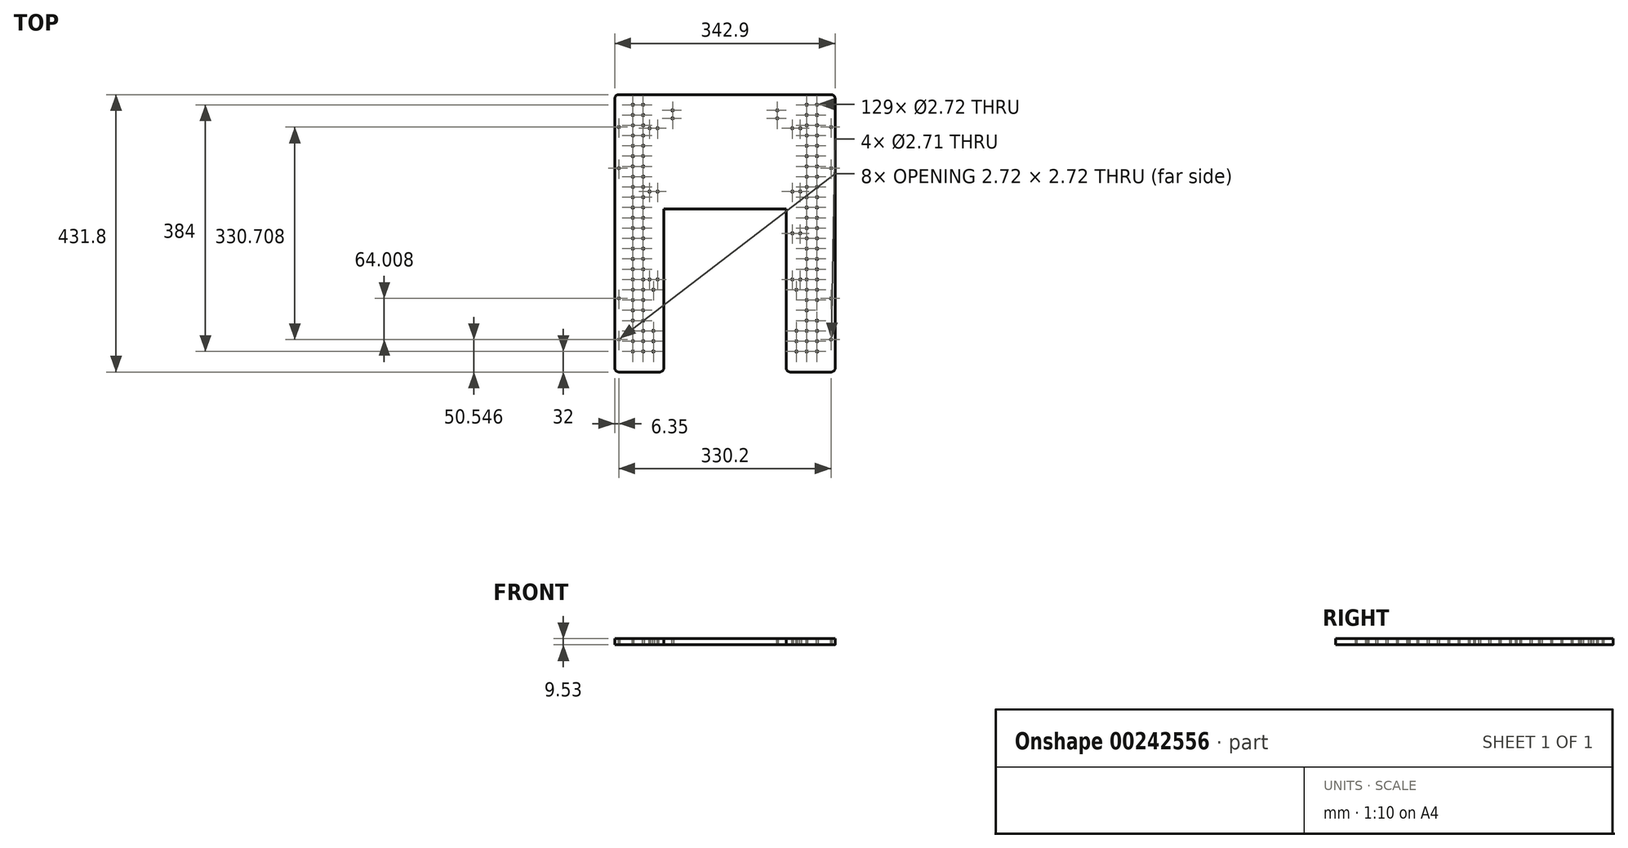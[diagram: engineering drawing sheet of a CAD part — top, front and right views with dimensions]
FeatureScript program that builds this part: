
annotation { "Feature Type Name" : "Feature", "Feature Type Description" : "" }
export const myFeature = defineFeature(function(context is Context, id is Id, definition is map)
    precondition{}
    {
        {
            var Q0;
            Q0=qCreatedBy(makeId("Top.planeOp"),FACE);
            var sketch = newSketch(context, id + "F0", { "sketchPlane" : qUnion([Q0])});
            skLineSegment(sketch, "E0.bottom", {"start": v(228.6, 228.6) * mm, "end": v(-228.6, 228.6) * mm, "construction": true});
            skLineSegment(sketch, "E0.top", {"start": v(228.6, -228.6) * mm, "end": v(-228.6, -228.6) * mm, "construction": true});
            skLineSegment(sketch, "E0.left", {"start": v(228.6, 228.6) * mm, "end": v(228.6, -228.6) * mm, "construction": true});
            skLineSegment(sketch, "E0.right", {"start": v(-228.6, 228.6) * mm, "end": v(-228.6, -228.6) * mm, "construction": true});
            skPoint(sketch, "E0.middle", {"position": v(0, 0) * mm});
            skLineSegment(sketch, "E1.bottom", {"start": v(-165.1, 215.9) * mm, "end": v(-101.6, 215.9) * mm});
            skLineSegment(sketch, "E1.top", {"start": v(-165.1, -215.9) * mm, "end": v(-101.6, -215.9) * mm});
            skLineSegment(sketch, "E1.left", {"start": v(-171.45, 209.55) * mm, "end": v(-171.45, -209.55) * mm});
            skLineSegment(sketch, "E1.right", {"start": v(-95.25, 209.55) * mm, "end": v(-95.25, -209.55) * mm});
            skLineSegment(sketch, "E2.bottom", {"start": v(-95.25, 215.9) * mm, "end": v(0, 215.9) * mm});
            skLineSegment(sketch, "E2.top", {"start": v(-95.25, 38.1) * mm, "end": v(0, 38.1) * mm});
            skLineSegment(sketch, "E2.left", {"start": v(-95.25, 215.9) * mm, "end": v(-95.25, 38.1) * mm});
            skLineSegment(sketch, "E2.right", {"start": v(0, 215.9) * mm, "end": v(0, 38.1) * mm});
            skLineSegment(sketch, "E3.MirrorCS", {"start": v(95.25, 215.9) * mm, "end": v(0, 215.9) * mm});
            skLineSegment(sketch, "E4.MirrorCS", {"start": v(95.25, 38.1) * mm, "end": v(0, 38.1) * mm});
            skLineSegment(sketch, "E5.MirrorCS", {"start": v(95.25, 215.9) * mm, "end": v(95.25, 38.1) * mm});
            skLineSegment(sketch, "E6.MirrorCS", {"start": v(95.25, 209.55) * mm, "end": v(95.25, -209.55) * mm});
            skLineSegment(sketch, "E7.MirrorCS", {"start": v(171.45, 209.55) * mm, "end": v(171.45, -209.55) * mm});
            skLineSegment(sketch, "E8.MirrorCS", {"start": v(165.1, -215.9) * mm, "end": v(101.6, -215.9) * mm});
            skLineSegment(sketch, "E9.MirrorCS", {"start": v(165.1, 215.9) * mm, "end": v(101.6, 215.9) * mm});
            skPoint(sketch, "E10.visualSharp", {"position": v(-171.45, 215.9) * mm});
            skArc(sketch, "E10.filletArc", {"start": v(-165.1, 215.9) * mm, "mid": v(-169.6, 214.04) * mm, "end": v(-171.45, 209.55) * mm});
            skPoint(sketch, "E11.visualSharp", {"position": v(-95.25, 215.9) * mm});
            skPoint(sketch, "E12.visualSharp", {"position": v(-171.45, -215.9) * mm});
            skArc(sketch, "E12.filletArc", {"start": v(-171.45, -209.55) * mm, "mid": v(-169.6, -214.04) * mm, "end": v(-165.1, -215.9) * mm});
            skPoint(sketch, "E13.visualSharp", {"position": v(-95.25, -215.9) * mm});
            skArc(sketch, "E13.filletArc", {"start": v(-101.6, -215.9) * mm, "mid": v(-97.1, -214.04) * mm, "end": v(-95.25, -209.55) * mm});
            skPoint(sketch, "E14.visualSharp", {"position": v(95.25, -215.9) * mm});
            skArc(sketch, "E14.filletArc", {"start": v(95.25, -209.55) * mm, "mid": v(97.1, -214.04) * mm, "end": v(101.6, -215.9) * mm});
            skPoint(sketch, "E15.visualSharp", {"position": v(171.45, -215.9) * mm});
            skArc(sketch, "E15.filletArc", {"start": v(165.1, -215.9) * mm, "mid": v(169.6, -214.04) * mm, "end": v(171.45, -209.55) * mm});
            skPoint(sketch, "E16.visualSharp", {"position": v(171.45, 215.9) * mm});
            skArc(sketch, "E16.filletArc", {"start": v(171.45, 209.55) * mm, "mid": v(169.6, 214.04) * mm, "end": v(165.1, 215.9) * mm});
            skPoint(sketch, "E17.visualSharp", {"position": v(95.25, 215.9) * mm});
            skCircle(sketch, "E18", {"center": v(-165.1, 165.35) * mm, "radius": 1.36 * mm});
            skCircle(sketch, "E19", {"center": v(-165.1, 101.35) * mm, "radius": 1.36 * mm});
            skPoint(sketch, "E20", {"position": v(-165.1, 133.35) * mm});
            skCircle(sketch, "E21.MirrorC", {"center": v(165.1, 165.35) * mm, "radius": 1.36 * mm});
            skCircle(sketch, "E22.MirrorC", {"center": v(165.1, 101.35) * mm, "radius": 1.36 * mm});
            skCircle(sketch, "E23.MirrorC", {"center": v(165.1, -101.35) * mm, "radius": 1.36 * mm});
            skCircle(sketch, "E24.MirrorC", {"center": v(165.1, -165.35) * mm, "radius": 1.36 * mm});
            skCircle(sketch, "E25.MirrorC", {"center": v(-165.1, -165.35) * mm, "radius": 1.36 * mm});
            skCircle(sketch, "E26.MirrorC", {"center": v(-165.1, -101.35) * mm, "radius": 1.36 * mm});
            skPoint(sketch, "E27", {"position": v(-111.25, -151.9) * mm});
            skPoint(sketch, "E28", {"position": v(-111.25, -87.9) * mm});
            skPoint(sketch, "E29", {"position": v(-111.25, -167.9) * mm});
            skPoint(sketch, "E30", {"position": v(-111.25, -183.9) * mm});
            skCircle(sketch, "E31", {"center": v(-117.25, 64.95) * mm, "radius": 1.36 * mm});
            skCircle(sketch, "E32", {"center": v(-111.25, -87.9) * mm, "radius": 1.36 * mm});
            skCircle(sketch, "E33", {"center": v(-111.25, -151.9) * mm, "radius": 1.36 * mm});
            skCircle(sketch, "E34", {"center": v(-111.25, -183.9) * mm, "radius": 1.36 * mm});
            skCircle(sketch, "E35", {"center": v(-111.25, -167.9) * mm, "radius": 1.36 * mm});
            skCircle(sketch, "E36", {"center": v(-104.75, 64.95) * mm, "radius": 1.36 * mm});
            skCircle(sketch, "E37", {"center": v(-117.25, -71.82) * mm, "radius": 1.36 * mm});
            skCircle(sketch, "E38", {"center": v(-104.75, -71.82) * mm, "radius": 1.36 * mm});
            skCircle(sketch, "E39", {"center": v(-117.25, 163.5) * mm, "radius": 1.36 * mm});
            skCircle(sketch, "E40", {"center": v(-104.75, 163.5) * mm, "radius": 1.36 * mm});
            skLineSegment(sketch, "E41", {"start": v(-101.6, 215.9) * mm, "end": v(-95.25, 215.9) * mm});
            skLineSegment(sketch, "E42", {"start": v(101.6, 215.9) * mm, "end": v(95.25, 215.9) * mm});
            skCircle(sketch, "E43", {"center": v(-81.47, 178.92) * mm, "radius": 1.36 * mm});
            skCircle(sketch, "E44", {"center": v(-81.47, 191.42) * mm, "radius": 1.36 * mm});
            skCircle(sketch, "E45.MirrorC", {"center": v(111.25, -183.9) * mm, "radius": 1.36 * mm});
            skCircle(sketch, "E46.MirrorC", {"center": v(111.25, -167.9) * mm, "radius": 1.36 * mm});
            skCircle(sketch, "E47.MirrorC", {"center": v(111.25, -151.9) * mm, "radius": 1.36 * mm});
            skCircle(sketch, "E48.MirrorC", {"center": v(111.25, -87.9) * mm, "radius": 1.36 * mm});
            skCircle(sketch, "E49.MirrorC", {"center": v(104.75, -71.82) * mm, "radius": 1.36 * mm});
            skCircle(sketch, "E50.MirrorC", {"center": v(117.25, -71.82) * mm, "radius": 1.36 * mm});
            skCircle(sketch, "E51.MirrorC", {"center": v(117.25, 0) * mm, "radius": 1.36 * mm});
            skCircle(sketch, "E52.MirrorC", {"center": v(104.75, 0) * mm, "radius": 1.36 * mm});
            skCircle(sketch, "E53.MirrorC", {"center": v(117.25, 64.95) * mm, "radius": 1.36 * mm});
            skCircle(sketch, "E54.MirrorC", {"center": v(104.75, 64.95) * mm, "radius": 1.36 * mm});
            skCircle(sketch, "E55.MirrorC", {"center": v(117.25, 163.5) * mm, "radius": 1.36 * mm});
            skCircle(sketch, "E56.MirrorC", {"center": v(104.75, 163.5) * mm, "radius": 1.36 * mm});
            skCircle(sketch, "E57.MirrorC", {"center": v(81.47, 178.92) * mm, "radius": 1.36 * mm});
            skCircle(sketch, "E58.MirrorC", {"center": v(81.47, 191.42) * mm, "radius": 1.36 * mm});
            skCircle(sketch, "E59.MirrorC", {"center": v(-143.25, -183.9) * mm, "radius": 1.36 * mm});
            skCircle(sketch, "E60.0.1.0", {"center": v(-143.25, -167.9) * mm, "radius": 1.36 * mm});
            skCircle(sketch, "E60.0.2.0", {"center": v(-143.25, -151.9) * mm, "radius": 1.36 * mm});
            skCircle(sketch, "E60.0.3.0", {"center": v(-143.25, -135.9) * mm, "radius": 1.36 * mm});
            skCircle(sketch, "E60.0.4.0", {"center": v(-143.25, -119.9) * mm, "radius": 1.36 * mm});
            skCircle(sketch, "E60.0.5.0", {"center": v(-143.25, -103.9) * mm, "radius": 1.36 * mm});
            skCircle(sketch, "E60.0.6.0", {"center": v(-143.25, -87.9) * mm, "radius": 1.36 * mm});
            skCircle(sketch, "E60.0.7.0", {"center": v(-143.25, -71.9) * mm, "radius": 1.36 * mm});
            skCircle(sketch, "E60.0.8.0", {"center": v(-143.25, -55.9) * mm, "radius": 1.36 * mm});
            skCircle(sketch, "E60.0.9.0", {"center": v(-143.25, -39.9) * mm, "radius": 1.36 * mm});
            skCircle(sketch, "E60.0.10.0", {"center": v(-143.25, -23.9) * mm, "radius": 1.36 * mm});
            skCircle(sketch, "E60.0.11.0", {"center": v(-143.25, -7.9) * mm, "radius": 1.36 * mm});
            skCircle(sketch, "E60.0.12.0", {"center": v(-143.25, 8.1) * mm, "radius": 1.36 * mm});
            skCircle(sketch, "E60.0.13.0", {"center": v(-143.25, 24.1) * mm, "radius": 1.36 * mm});
            skCircle(sketch, "E60.0.14.0", {"center": v(-143.25, 40.1) * mm, "radius": 1.36 * mm});
            skCircle(sketch, "E60.0.15.0", {"center": v(-143.25, 56.1) * mm, "radius": 1.36 * mm});
            skCircle(sketch, "E60.0.16.0", {"center": v(-143.25, 72.1) * mm, "radius": 1.36 * mm});
            skCircle(sketch, "E60.0.17.0", {"center": v(-143.25, 88.1) * mm, "radius": 1.36 * mm});
            skCircle(sketch, "E60.0.18.0", {"center": v(-143.25, 104.1) * mm, "radius": 1.36 * mm});
            skCircle(sketch, "E60.0.19.0", {"center": v(-143.25, 120.1) * mm, "radius": 1.36 * mm});
            skCircle(sketch, "E60.0.20.0", {"center": v(-143.25, 136.1) * mm, "radius": 1.36 * mm});
            skCircle(sketch, "E60.0.21.0", {"center": v(-143.25, 152.1) * mm, "radius": 1.36 * mm});
            skCircle(sketch, "E60.0.22.0", {"center": v(-143.25, 168.1) * mm, "radius": 1.36 * mm});
            skCircle(sketch, "E60.0.23.0", {"center": v(-143.25, 184.1) * mm, "radius": 1.36 * mm});
            skCircle(sketch, "E60.0.24.0", {"center": v(-143.25, 200.1) * mm, "radius": 1.36 * mm});
            skLineSegment(sketch, "E60.direction1", {"start": v(-143.25, -183.9) * mm, "end": v(-127.25, -183.9) * mm, "construction": true});
            skLineSegment(sketch, "E60.direction2", {"start": v(-143.25, -183.9) * mm, "end": v(-143.25, -167.9) * mm, "construction": true});
            skCircle(sketch, "E61.0.1.0", {"center": v(-127.25, -183.9) * mm, "radius": 1.36 * mm});
            skCircle(sketch, "E61.0.1.1", {"center": v(-127.25, -167.9) * mm, "radius": 1.36 * mm});
            skCircle(sketch, "E61.0.1.2", {"center": v(-127.25, -151.9) * mm, "radius": 1.36 * mm});
            skCircle(sketch, "E61.0.1.3", {"center": v(-127.25, -135.9) * mm, "radius": 1.36 * mm});
            skCircle(sketch, "E61.0.1.4", {"center": v(-127.25, -119.9) * mm, "radius": 1.36 * mm});
            skCircle(sketch, "E61.0.1.5", {"center": v(-127.25, -103.9) * mm, "radius": 1.36 * mm});
            skCircle(sketch, "E61.0.1.6", {"center": v(-127.25, -87.9) * mm, "radius": 1.36 * mm});
            skCircle(sketch, "E61.0.1.7", {"center": v(-127.25, -71.9) * mm, "radius": 1.36 * mm});
            skCircle(sketch, "E61.0.1.8", {"center": v(-127.25, -55.9) * mm, "radius": 1.36 * mm});
            skCircle(sketch, "E61.0.1.9", {"center": v(-127.25, -39.9) * mm, "radius": 1.36 * mm});
            skCircle(sketch, "E61.0.1.10", {"center": v(-127.25, -23.9) * mm, "radius": 1.36 * mm});
            skCircle(sketch, "E61.0.1.11", {"center": v(-127.25, -7.9) * mm, "radius": 1.36 * mm});
            skCircle(sketch, "E61.0.1.12", {"center": v(-127.25, 8.1) * mm, "radius": 1.36 * mm});
            skCircle(sketch, "E61.0.1.13", {"center": v(-127.25, 24.1) * mm, "radius": 1.36 * mm});
            skCircle(sketch, "E61.0.1.14", {"center": v(-127.25, 40.1) * mm, "radius": 1.36 * mm});
            skCircle(sketch, "E61.0.1.15", {"center": v(-127.25, 56.1) * mm, "radius": 1.36 * mm});
            skCircle(sketch, "E61.0.1.16", {"center": v(-127.25, 72.1) * mm, "radius": 1.36 * mm});
            skCircle(sketch, "E61.0.1.17", {"center": v(-127.25, 88.1) * mm, "radius": 1.36 * mm});
            skCircle(sketch, "E61.0.1.18", {"center": v(-127.25, 104.1) * mm, "radius": 1.36 * mm});
            skCircle(sketch, "E61.0.1.19", {"center": v(-127.25, 120.1) * mm, "radius": 1.36 * mm});
            skCircle(sketch, "E61.0.1.20", {"center": v(-127.25, 136.1) * mm, "radius": 1.36 * mm});
            skCircle(sketch, "E61.0.1.21", {"center": v(-127.25, 152.1) * mm, "radius": 1.36 * mm});
            skCircle(sketch, "E61.0.1.22", {"center": v(-127.25, 168.1) * mm, "radius": 1.36 * mm});
            skCircle(sketch, "E61.0.1.23", {"center": v(-127.25, 184.1) * mm, "radius": 1.36 * mm});
            skCircle(sketch, "E61.0.1.24", {"center": v(-127.25, 200.1) * mm, "radius": 1.36 * mm});
            skCircle(sketch, "E62.MirrorC", {"center": v(127.25, -183.9) * mm, "radius": 1.36 * mm});
            skCircle(sketch, "E63.MirrorC", {"center": v(143.25, -183.9) * mm, "radius": 1.36 * mm});
            skCircle(sketch, "E64.MirrorC", {"center": v(143.25, -167.9) * mm, "radius": 1.36 * mm});
            skCircle(sketch, "E65.MirrorC", {"center": v(127.25, -167.9) * mm, "radius": 1.36 * mm});
            skCircle(sketch, "E66.MirrorC", {"center": v(127.25, -151.9) * mm, "radius": 1.36 * mm});
            skCircle(sketch, "E67.MirrorC", {"center": v(143.25, -151.9) * mm, "radius": 1.36 * mm});
            skCircle(sketch, "E68.MirrorC", {"center": v(143.25, -135.9) * mm, "radius": 1.36 * mm});
            skCircle(sketch, "E69.MirrorC", {"center": v(127.25, -135.9) * mm, "radius": 1.36 * mm});
            skCircle(sketch, "E70.MirrorC", {"center": v(127.25, -119.9) * mm, "radius": 1.36 * mm});
            skCircle(sketch, "E71.MirrorC", {"center": v(127.25, -103.9) * mm, "radius": 1.36 * mm});
            skCircle(sketch, "E72.MirrorC", {"center": v(127.25, -87.9) * mm, "radius": 1.36 * mm});
            skCircle(sketch, "E73.MirrorC", {"center": v(143.25, -103.9) * mm, "radius": 1.36 * mm});
            skCircle(sketch, "E74.MirrorC", {"center": v(143.25, -87.9) * mm, "radius": 1.36 * mm});
            skCircle(sketch, "E75.MirrorC", {"center": v(143.25, -71.9) * mm, "radius": 1.36 * mm});
            skCircle(sketch, "E76.MirrorC", {"center": v(143.25, -55.9) * mm, "radius": 1.36 * mm});
            skCircle(sketch, "E77.MirrorC", {"center": v(127.25, -71.9) * mm, "radius": 1.36 * mm});
            skCircle(sketch, "E78.MirrorC", {"center": v(127.25, -55.9) * mm, "radius": 1.36 * mm});
            skCircle(sketch, "E79.MirrorC", {"center": v(143.25, -39.9) * mm, "radius": 1.36 * mm});
            skCircle(sketch, "E80.MirrorC", {"center": v(127.25, -39.9) * mm, "radius": 1.36 * mm});
            skCircle(sketch, "E81.MirrorC", {"center": v(143.25, -23.9) * mm, "radius": 1.36 * mm});
            skCircle(sketch, "E82.MirrorC", {"center": v(127.25, -23.9) * mm, "radius": 1.36 * mm});
            skCircle(sketch, "E83.MirrorC", {"center": v(127.25, -7.9) * mm, "radius": 1.36 * mm});
            skCircle(sketch, "E84.MirrorC", {"center": v(143.25, -7.9) * mm, "radius": 1.36 * mm});
            skCircle(sketch, "E85.MirrorC", {"center": v(143.25, 8.1) * mm, "radius": 1.36 * mm});
            skCircle(sketch, "E86.MirrorC", {"center": v(127.25, 8.1) * mm, "radius": 1.36 * mm});
            skCircle(sketch, "E87.MirrorC", {"center": v(127.25, 24.1) * mm, "radius": 1.36 * mm});
            skCircle(sketch, "E88.MirrorC", {"center": v(143.25, 24.1) * mm, "radius": 1.36 * mm});
            skCircle(sketch, "E89.MirrorC", {"center": v(143.25, 40.1) * mm, "radius": 1.36 * mm});
            skCircle(sketch, "E90.MirrorC", {"center": v(127.25, 40.1) * mm, "radius": 1.36 * mm});
            skCircle(sketch, "E91.MirrorC", {"center": v(127.25, 56.1) * mm, "radius": 1.36 * mm});
            skCircle(sketch, "E92.MirrorC", {"center": v(143.25, 56.1) * mm, "radius": 1.36 * mm});
            skCircle(sketch, "E93.MirrorC", {"center": v(143.25, 72.1) * mm, "radius": 1.36 * mm});
            skCircle(sketch, "E94.MirrorC", {"center": v(127.25, 72.1) * mm, "radius": 1.36 * mm});
            skCircle(sketch, "E95.MirrorC", {"center": v(143.25, 88.1) * mm, "radius": 1.36 * mm});
            skCircle(sketch, "E96.MirrorC", {"center": v(127.25, 88.1) * mm, "radius": 1.36 * mm});
            skCircle(sketch, "E97.MirrorC", {"center": v(127.25, 104.1) * mm, "radius": 1.36 * mm});
            skCircle(sketch, "E98.MirrorC", {"center": v(143.25, 104.1) * mm, "radius": 1.36 * mm});
            skCircle(sketch, "E99.MirrorC", {"center": v(143.25, 120.1) * mm, "radius": 1.36 * mm});
            skCircle(sketch, "E100.MirrorC", {"center": v(127.25, 120.1) * mm, "radius": 1.36 * mm});
            skCircle(sketch, "E101.MirrorC", {"center": v(143.25, 200.1) * mm, "radius": 1.36 * mm});
            skCircle(sketch, "E102.MirrorC", {"center": v(143.25, 184.1) * mm, "radius": 1.36 * mm});
            skCircle(sketch, "E103.MirrorC", {"center": v(143.25, 168.1) * mm, "radius": 1.36 * mm});
            skCircle(sketch, "E104.MirrorC", {"center": v(143.25, 152.1) * mm, "radius": 1.36 * mm});
            skCircle(sketch, "E105.MirrorC", {"center": v(143.25, 136.1) * mm, "radius": 1.36 * mm});
            skCircle(sketch, "E106.MirrorC", {"center": v(127.25, 136.1) * mm, "radius": 1.36 * mm});
            skCircle(sketch, "E107.MirrorC", {"center": v(127.25, 152.1) * mm, "radius": 1.36 * mm});
            skCircle(sketch, "E108.MirrorC", {"center": v(127.25, 168.1) * mm, "radius": 1.36 * mm});
            skCircle(sketch, "E109.MirrorC", {"center": v(127.25, 184.1) * mm, "radius": 1.36 * mm});
            skCircle(sketch, "E110.MirrorC", {"center": v(127.25, 200.1) * mm, "radius": 1.36 * mm});
            skSolve(sketch);
        }
        {
            var Q0;
            Q0=makeQuery(id+"F0.imprint","IMPRINT",FACE,{"disambiguationData":[TD([[makeQuery(id+"F0.imprint","IMPRINT",EDGE,{"derivedFrom":sQuery(id+"F0.wireOp",EDGE,"E2.bottom")}),-1.0]])]});
            var Q1;
            Q1=makeQuery(id+"F0.imprint","IMPRINT",FACE,{"disambiguationData":[TD([[makeQuery(id+"F0.imprint","IMPRINT",EDGE,{"derivedFrom":sQuery(id+"F0.wireOp",EDGE,"E2.right")}),1.0]])]});
            var Q2;
            Q2=makeQuery(id+"F0.imprint","IMPRINT",FACE,{"disambiguationData":[TD([[makeQuery(id+"F0.imprint","IMPRINT",EDGE,{"derivedFrom":sQuery(id+"F0.wireOp",EDGE,"E1.bottom")}),-1.0]])]});
            var Q3;
            Q3=makeQuery(id+"F0.imprint","IMPRINT",FACE,{"disambiguationData":[TD([[makeQuery(id+"F0.imprint","IMPRINT",EDGE,{"derivedFrom":sQuery(id+"F0.wireOp",EDGE,"E18")}),1.0]])]});
            var Q4;
            Q4=makeQuery(id+"F0.imprint","IMPRINT",FACE,{"disambiguationData":[TD([[makeQuery(id+"F0.imprint","IMPRINT",EDGE,{"derivedFrom":sQuery(id+"F0.wireOp",EDGE,"E19")}),1.0]])]});
            var Q5;
            Q5=makeQuery(id+"F0.imprint","IMPRINT",FACE,{"disambiguationData":[TD([[makeQuery(id+"F0.imprint","IMPRINT",EDGE,{"derivedFrom":sQuery(id+"F0.wireOp",EDGE,"E26.MirrorC")}),-1.0]])]});
            var Q6;
            Q6=makeQuery(id+"F0.imprint","IMPRINT",FACE,{"disambiguationData":[TD([[makeQuery(id+"F0.imprint","IMPRINT",EDGE,{"derivedFrom":sQuery(id+"F0.wireOp",EDGE,"E25.MirrorC")}),-1.0]])]});
            var Q7;
            Q7=makeQuery(id+"F0.imprint","IMPRINT",FACE,{"disambiguationData":[TD([[makeQuery(id+"F0.imprint","IMPRINT",EDGE,{"derivedFrom":sQuery(id+"F0.wireOp",EDGE,"E24.MirrorC")}),1.0]])]});
            var Q8;
            Q8=makeQuery(id+"F0.imprint","IMPRINT",FACE,{"disambiguationData":[TD([[makeQuery(id+"F0.imprint","IMPRINT",EDGE,{"derivedFrom":sQuery(id+"F0.wireOp",EDGE,"E23.MirrorC")}),1.0]])]});
            var Q9;
            Q9=makeQuery(id+"F0.imprint","IMPRINT",FACE,{"disambiguationData":[TD([[makeQuery(id+"F0.imprint","IMPRINT",EDGE,{"derivedFrom":sQuery(id+"F0.wireOp",EDGE,"E7.MirrorCS")}),-1.0]])]});
            var Q10;
            Q10=makeQuery(id+"F0.imprint","IMPRINT",FACE,{"disambiguationData":[TD([[makeQuery(id+"F0.imprint","IMPRINT",EDGE,{"derivedFrom":sQuery(id+"F0.wireOp",EDGE,"E22.MirrorC")}),-1.0]])]});
            var Q11;
            Q11=makeQuery(id+"F0.imprint","IMPRINT",FACE,{"disambiguationData":[TD([[makeQuery(id+"F0.imprint","IMPRINT",EDGE,{"derivedFrom":sQuery(id+"F0.wireOp",EDGE,"E21.MirrorC")}),-1.0]])]});
            extrude(context, id + "F1", {"entities" : qUnion([Q0, Q1, Q2, Q3, Q4, Q5, Q6, Q7, Q8, Q9, Q10, Q11]), "depth" : 9.52 * mm});
        }
        {
            var Q0;
            Q0=sQuery(id+"F0.wireOp",VERTEX,"E26.MirrorC.center");
            var Q1;
            Q1=sQuery(id+"F0.wireOp",VERTEX,"E25.MirrorC.center");
            var Q2;
            Q2=sQuery(id+"F0.wireOp",VERTEX,"E18.center");
            var Q3;
            Q3=sQuery(id+"F0.wireOp",VERTEX,"E19.center");
            var Q4;
            Q4=sQuery(id+"F0.wireOp",VERTEX,"E21.MirrorC.center");
            var Q5;
            Q5=sQuery(id+"F0.wireOp",VERTEX,"E22.MirrorC.center");
            var Q6;
            Q6=sQuery(id+"F0.wireOp",VERTEX,"E23.MirrorC.center");
            var Q7;
            Q7=sQuery(id+"F0.wireOp",VERTEX,"E24.MirrorC.center");
            var Q8;
            Q8=sQuery(id+"F0.wireOp",VERTEX,"E27");
            var Q9;
            Q9=sQuery(id+"F0.wireOp",VERTEX,"E29");
            var Q10;
            Q10=sQuery(id+"F0.wireOp",VERTEX,"E30");
            var Q11;
            Q11=sQuery(id+"F0.wireOp",VERTEX,"E28");
            var Q12;
            Q12=makeQuery(id+"F1.opExtrude","SWEPT_BODY",BODY,{"disambiguationData":[OSD([sQuery(id+"F0.wireOp",EDGE,"E1.bottom"),sQuery(id+"F0.wireOp",EDGE,"E1.top"),sQuery(id+"F0.wireOp",EDGE,"E1.left"),sQuery(id+"F0.wireOp",EDGE,"E1.right"),sQuery(id+"F0.wireOp",EDGE,"E2.bottom"),sQuery(id+"F0.wireOp",EDGE,"E2.top"),sQuery(id+"F0.wireOp",EDGE,"E3.MirrorCS"),sQuery(id+"F0.wireOp",EDGE,"E4.MirrorCS"),sQuery(id+"F0.wireOp",EDGE,"E6.MirrorCS"),sQuery(id+"F0.wireOp",EDGE,"E7.MirrorCS"),sQuery(id+"F0.wireOp",EDGE,"E8.MirrorCS"),sQuery(id+"F0.wireOp",EDGE,"E9.MirrorCS"),sQuery(id+"F0.wireOp",EDGE,"E10.filletArc"),sQuery(id+"F0.wireOp",EDGE,"E11.filletArc"),sQuery(id+"F0.wireOp",EDGE,"E12.filletArc"),sQuery(id+"F0.wireOp",EDGE,"E13.filletArc"),sQuery(id+"F0.wireOp",EDGE,"E14.filletArc"),sQuery(id+"F0.wireOp",EDGE,"E15.filletArc"),sQuery(id+"F0.wireOp",EDGE,"E16.filletArc"),sQuery(id+"F0.wireOp",EDGE,"E17.filletArc")])]});
            hole(context, id + "F2", {"style" : HoleStyle.SIMPLE, "endStyle" : HoleEndStyle.THROUGH, "oppositeDirection" : true, "standardTappedOrClearance" : lookupTablePath({ "standard" : "ANSI", "engagement" : "75%", "pitch" : "32 tpi", "size" : "#6", "type" : "Tapped" }), "standardBlindInLast" : lookupTablePath({ "standard" : "ANSI", "engagement" : "75%", "pitch" : "32 tpi", "size" : "#6", "type" : "Tapped" }), "holeDiameter" : 2.7 * mm, "showTappedDepth" : true, "isTappedThrough" : true, "tappedDepth" : 12.7 * mm, "tapClearance" : 3, "locations" : qUnion([Q0, Q1, Q2, Q3, Q4, Q5, Q6, Q7, Q8, Q9, Q10, Q11]), "scope" : qUnion([Q12]), "majorDiameter" : 3.5 * mm});
        }
    });
